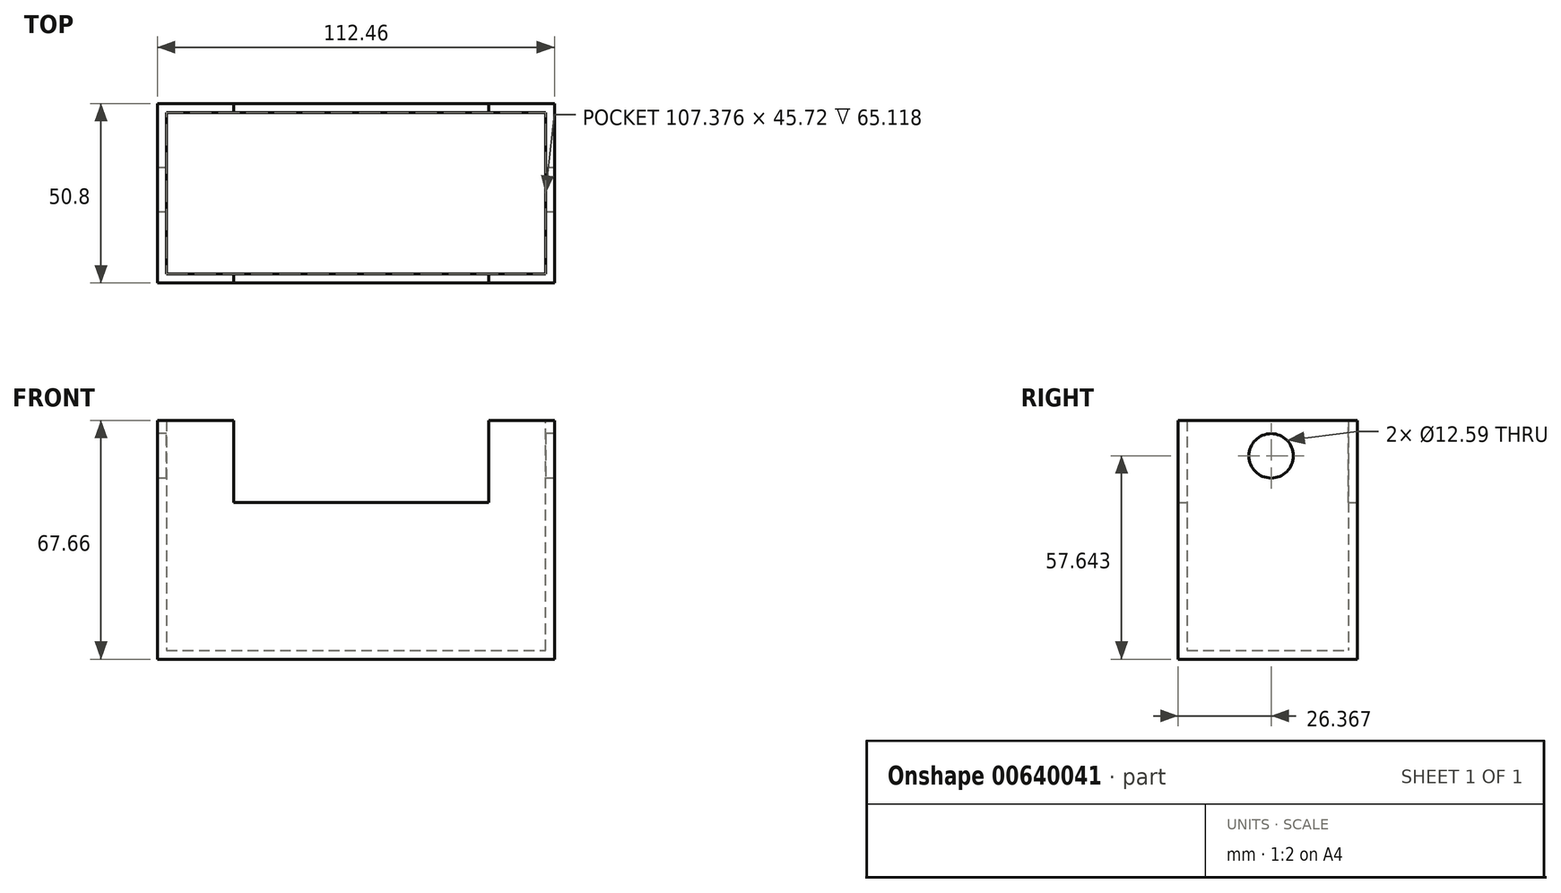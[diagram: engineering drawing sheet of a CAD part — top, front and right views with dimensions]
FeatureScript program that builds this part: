
annotation { "Feature Type Name" : "Feature", "Feature Type Description" : "" }
export const myFeature = defineFeature(function(context is Context, id is Id, definition is map)
    precondition{}
    {
        {
            var Q0;
            Q0=qCreatedBy(makeId("Front.planeOp"),FACE);
            var sketch = newSketch(context, id + "F0", { "sketchPlane" : qUnion([Q0])});
            skLineSegment(sketch, "E0", {"start": v(-47.47, 44.7) * mm, "end": v(-47.47, -22.95) * mm});
            skLineSegment(sketch, "E1", {"start": v(-47.47, -22.95) * mm, "end": v(64.99, -22.95) * mm});
            skLineSegment(sketch, "E2", {"start": v(64.99, -22.95) * mm, "end": v(64.99, 44.7) * mm});
            skLineSegment(sketch, "E3", {"start": v(64.99, 44.7) * mm, "end": v(46.37, 44.7) * mm});
            skLineSegment(sketch, "E4", {"start": v(46.37, 44.7) * mm, "end": v(46.37, 21.48) * mm});
            skLineSegment(sketch, "E5", {"start": v(46.37, 21.48) * mm, "end": v(-25.9, 21.48) * mm});
            skLineSegment(sketch, "E6", {"start": v(-25.9, 21.48) * mm, "end": v(-25.9, 44.7) * mm});
            skLineSegment(sketch, "E7", {"start": v(-25.9, 44.7) * mm, "end": v(-47.47, 44.7) * mm});
            skSolve(sketch);
        }
        {
            var Q0;
            Q0=makeQuery(id+"F0.imprint","IMPRINT",FACE,{"disambiguationData":[TD([[makeQuery(id+"F0.imprint","IMPRINT",EDGE,{"derivedFrom":sQuery(id+"F0.wireOp",EDGE,"E0")}),1.0]])]});
            extrude(context, id + "F1", {"entities" : qUnion([Q0]), "depth" : 50.8 * mm, "offsetDistance" : 25.4 * mm});
        }
        {
            var Q0;
            Q0=makeQuery(id+"F1.opExtrude","SWEPT_FACE",FACE,{"disambiguationData":[OSD([sQuery(id+"F0.wireOp",EDGE,"E5")])]});
            var Q1;
            Q1=makeQuery(id+"F1.opExtrude","SWEPT_FACE",FACE,{"disambiguationData":[OSD([sQuery(id+"F0.wireOp",EDGE,"E7")])]});
            var Q2;
            Q2=makeQuery(id+"F1.opExtrude","SWEPT_FACE",FACE,{"disambiguationData":[OSD([sQuery(id+"F0.wireOp",EDGE,"E3")])]});
            var Q3;
            Q3=makeQuery(id+"F1.opExtrude","SWEPT_FACE",FACE,{"disambiguationData":[OSD([sQuery(id+"F0.wireOp",EDGE,"E4")])]});
            var Q4;
            Q4=makeQuery(id+"F1.opExtrude","SWEPT_FACE",FACE,{"disambiguationData":[OSD([sQuery(id+"F0.wireOp",EDGE,"E6")])]});
            shell(context, id + "F2", {"entities" : qUnion([Q0, Q1, Q2, Q3, Q4]), "thickness" : 2.54 * mm});
        }
        {
            var Q0;
            Q0=makeQuery(id+"F1.opExtrude","SWEPT_FACE",FACE,{"disambiguationData":[OSD([sQuery(id+"F0.wireOp",EDGE,"E0")])]});
            var sketch = newSketch(context, id + "F3", { "sketchPlane" : qUnion([Q0])});
            skCircle(sketch, "E8", {"center": v(24.43, 34.7) * mm, "radius": 6.3 * mm});
            skSolve(sketch);
        }
        {
            var Q0;
            Q0=makeQuery(id+"F3.imprint","IMPRINT",FACE,{"disambiguationData":[TD([[makeQuery(id+"F3.imprint","IMPRINT",EDGE,{"derivedFrom":sQuery(id+"F3.wireOp",EDGE,"E8")}),1.0]])]});
            extrude(context, id + "F4", {"entities" : qUnion([Q0]), "operationType" : NewBodyOperationType.REMOVE, "oppositeDirection" : true, "depth" : 322.58 * mm, "offsetDistance" : 25.4 * mm});
        }
    });
